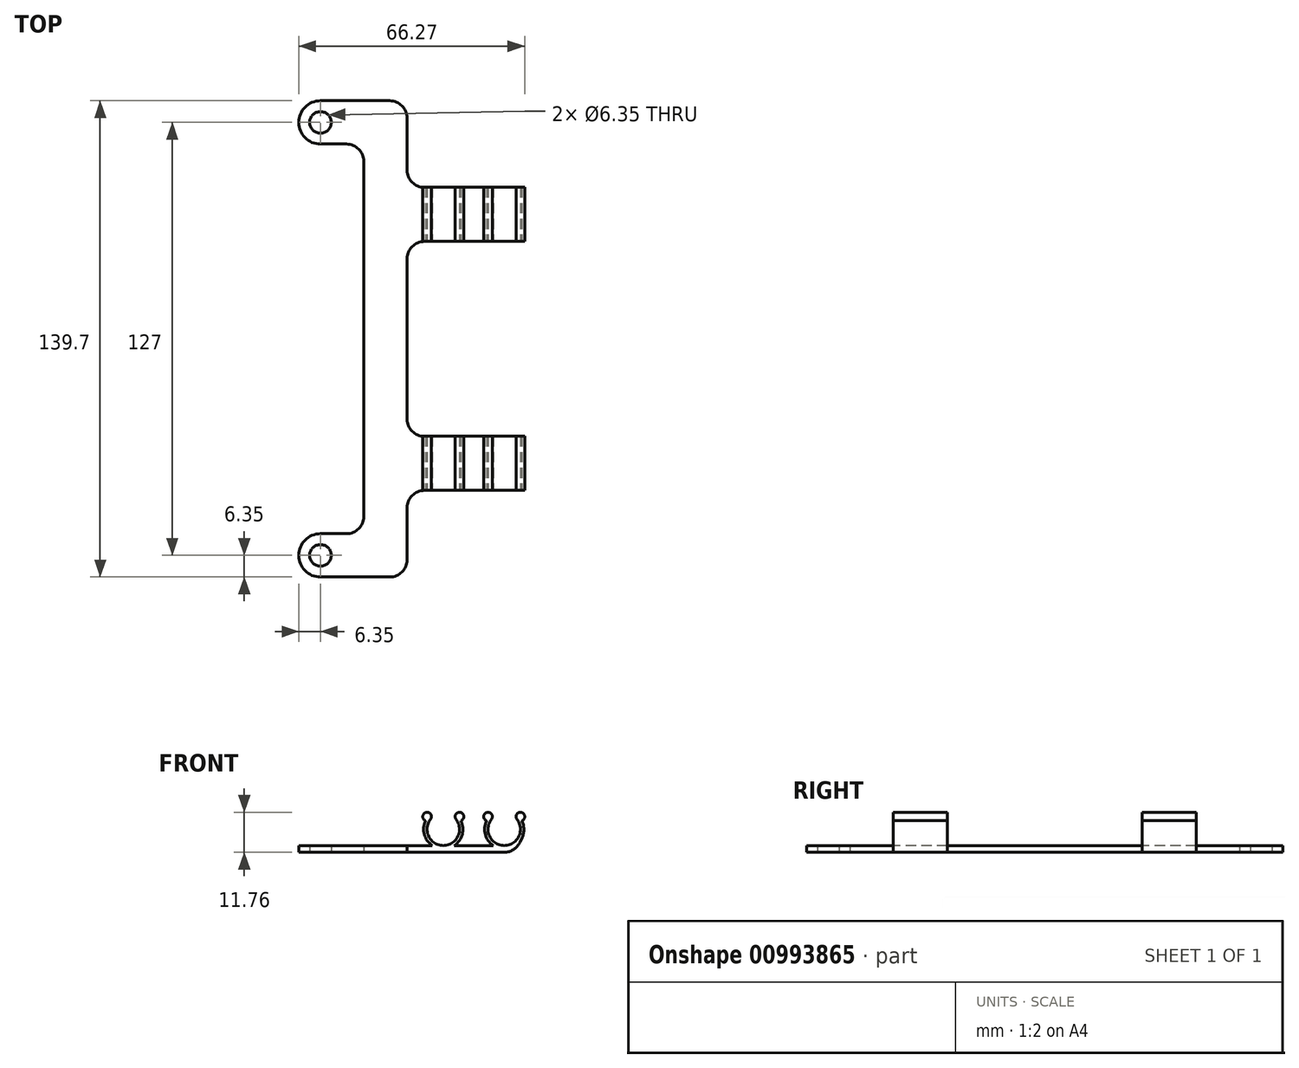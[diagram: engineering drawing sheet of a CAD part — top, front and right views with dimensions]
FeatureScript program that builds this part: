
annotation { "Feature Type Name" : "Feature", "Feature Type Description" : "" }
export const myFeature = defineFeature(function(context is Context, id is Id, definition is map)
    precondition{}
    {
        {
            var Q0;
            Q0=qCreatedBy(makeId("Top.planeOp"),FACE);
            var sketch = newSketch(context, id + "F0", { "sketchPlane" : qUnion([Q0])});
            skLineSegment(sketch, "E0", {"start": v(6.35, 0) * mm, "end": v(31.75, 0) * mm});
            skLineSegment(sketch, "E1", {"start": v(31.75, 0) * mm, "end": v(31.75, 25.4) * mm});
            skLineSegment(sketch, "E2", {"start": v(31.75, 25.4) * mm, "end": v(63.5, 25.4) * mm});
            skLineSegment(sketch, "E3", {"start": v(63.5, 25.4) * mm, "end": v(63.5, 41.28) * mm});
            skLineSegment(sketch, "E4", {"start": v(63.5, 41.28) * mm, "end": v(31.75, 41.28) * mm});
            skLineSegment(sketch, "E5", {"start": v(31.75, 41.28) * mm, "end": v(31.75, 98.42) * mm});
            skLineSegment(sketch, "E6", {"start": v(31.75, 98.42) * mm, "end": v(63.5, 98.42) * mm});
            skLineSegment(sketch, "E7", {"start": v(63.5, 98.42) * mm, "end": v(63.5, 114.3) * mm});
            skLineSegment(sketch, "E8", {"start": v(31.75, 114.3) * mm, "end": v(31.75, 139.7) * mm});
            skLineSegment(sketch, "E9", {"start": v(31.75, 139.7) * mm, "end": v(6.35, 139.7) * mm});
            skLineSegment(sketch, "E10", {"start": v(6.35, 127) * mm, "end": v(19.05, 127) * mm});
            skLineSegment(sketch, "E11", {"start": v(19.05, 127) * mm, "end": v(19.05, 12.7) * mm});
            skLineSegment(sketch, "E12", {"start": v(19.05, 12.7) * mm, "end": v(6.35, 12.7) * mm});
            skLineSegment(sketch, "E13", {"start": v(31.75, 69.85) * mm, "end": v(19.05, 69.85) * mm, "construction": true});
            skLineSegment(sketch, "E14", {"start": v(0, 133.35) * mm, "end": v(31.75, 133.35) * mm, "construction": true});
            skLineSegment(sketch, "E15", {"start": v(0, 6.35) * mm, "end": v(31.75, 6.35) * mm, "construction": true});
            skCircle(sketch, "E16", {"center": v(6.35, 133.35) * mm, "radius": 3.18 * mm});
            skArc(sketch, "E17", {"start": v(6.35, 139.7) * mm, "mid": v(0, 133.35) * mm, "end": v(6.35, 127) * mm});
            skPoint(sketch, "E18.orphan", {"position": v(0, 139.7) * mm});
            skPoint(sketch, "E19.orphan", {"position": v(0, 127) * mm});
            skArc(sketch, "E20", {"start": v(6.35, 12.7) * mm, "mid": v(0, 6.35) * mm, "end": v(6.35, 0) * mm});
            skCircle(sketch, "E21", {"center": v(6.35, 6.35) * mm, "radius": 3.18 * mm});
            skPoint(sketch, "E22.orphan", {"position": v(0, 12.7) * mm});
            skPoint(sketch, "E23.end.orphan", {"position": v(0, 0) * mm});
            skLineSegment(sketch, "E24", {"start": v(31.75, 114.3) * mm, "end": v(63.5, 114.3) * mm});
            skSolve(sketch);
        }
        {
            var Q0;
            Q0=qSketchRegion(id+"F0",true);
            extrude(context, id + "F1", {"entities" : qUnion([Q0]), "depth" : 2 * mm, "offsetDistance" : 25.4 * mm});
        }
        {
            var Q0;
            Q0=makeQuery(id+"F1.opExtrude","SWEPT_FACE",FACE,{"disambiguationData":[OSD([sQuery(id+"F0.wireOp",EDGE,"E2")])]});
            var sketch = newSketch(context, id + "F2", { "sketchPlane" : qUnion([Q0])});
            skArc(sketch, "E25", {"start": v(55.08, 9.3) * mm, "mid": v(60.26, 1) * mm, "end": v(65.43, 9.3) * mm});
            skArc(sketch, "E26", {"start": v(56.5, 9.7) * mm, "mid": v(60.26, 2) * mm, "end": v(64, 9.7) * mm});
            skLineSegment(sketch, "E27", {"start": v(60.26, 6.76) * mm, "end": v(60.26, 20.65) * mm, "construction": true});
            skLineSegment(sketch, "E28.0", {"start": v(64, 9.7) * mm, "end": v(64, 11.14) * mm, "construction": true});
            skLineSegment(sketch, "E29.0", {"start": v(56.5, 9.7) * mm, "end": v(56.5, 11.14) * mm, "construction": true});
            skArc(sketch, "E30", {"start": v(56.5, 9.7) * mm, "mid": v(55.16, 11.7) * mm, "end": v(55.08, 9.3) * mm});
            skArc(sketch, "E31.MirrorC", {"start": v(64, 9.7) * mm, "mid": v(65.35, 11.7) * mm, "end": v(65.43, 9.3) * mm});
            skLineSegment(sketch, "E32", {"start": v(51.32, 2) * mm, "end": v(51.32, 33.75) * mm, "construction": true});
            skArc(sketch, "E33.MirrorCS", {"start": v(38.63, 9.7) * mm, "mid": v(37.29, 11.7) * mm, "end": v(37.2, 9.3) * mm});
            skArc(sketch, "E34.MirrorCS", {"start": v(47.56, 9.3) * mm, "mid": v(42.38, 1) * mm, "end": v(37.2, 9.3) * mm});
            skArc(sketch, "E35.MirrorCS", {"start": v(46.13, 9.7) * mm, "mid": v(47.48, 11.7) * mm, "end": v(47.56, 9.3) * mm});
            skArc(sketch, "E36.MirrorCS", {"start": v(46.13, 9.7) * mm, "mid": v(42.38, 2) * mm, "end": v(38.63, 9.7) * mm});
            skPoint(sketch, "E37", {"position": v(51.32, 2) * mm});
            skSolve(sketch);
        }
        {
            var Q0;
            Q0=qSketchRegion(id+"F2",true);
            var Q1;
            Q1=makeQuery(id+"F1.opExtrude","SWEPT_FACE",FACE,{"disambiguationData":[OSD([sQuery(id+"F0.wireOp",EDGE,"E24")])]});
            extrude(context, id + "F3", {"entities" : qUnion([Q0]), "operationType" : NewBodyOperationType.ADD, "endBound" : BoundingType.UP_TO_SURFACE, "oppositeDirection" : true, "depth" : 25.4 * mm, "endBoundEntityFace" : qUnion([Q1]), "offsetDistance" : 25.4 * mm});
        }
        {
            var Q0;
            Q0=makeQuery(id+"F3.boolean.opBoolean","MERGE",FACE,{"derivedFrom":[makeQuery(id+"F1.opExtrude","SWEPT_FACE",FACE,{"disambiguationData":[OSD([sQuery(id+"F0.wireOp",EDGE,"E2")])]}),makeQuery(id+"F3.opExtrude","CAP_FACE",FACE,{"disambiguationData":[OSD([sQuery(id+"F2.wireOp",EDGE,"E25"),sQuery(id+"F2.wireOp",EDGE,"E26"),sQuery(id+"F2.wireOp",EDGE,"E30"),sQuery(id+"F2.wireOp",EDGE,"E31.MirrorC")])],"isStart":true}),makeQuery(id+"F3.opExtrude","CAP_FACE",FACE,{"disambiguationData":[OSD([sQuery(id+"F2.wireOp",EDGE,"E33.MirrorCS"),sQuery(id+"F2.wireOp",EDGE,"E34.MirrorCS"),sQuery(id+"F2.wireOp",EDGE,"E35.MirrorCS"),sQuery(id+"F2.wireOp",EDGE,"E36.MirrorCS")])],"isStart":true})]});
            var sketch = newSketch(context, id + "F4", { "sketchPlane" : qUnion([Q0])});
            skLineSegment(sketch, "E38", {"start": v(65.5, 4.37) * mm, "end": v(63.5, 0) * mm});
            skLineSegment(sketch, "E39", {"start": v(65.5, 4.37) * mm, "end": v(63.5, 2) * mm});
            skLineSegment(sketch, "E40", {"start": v(63.5, 2) * mm, "end": v(63.5, 0) * mm});
            skSolve(sketch);
        }
        {
            var Q0;
            Q0=qSketchRegion(id+"F4",true);
            var Q1;
            Q1=makeQuery(id+"F3.boolean.opBoolean","MERGE",FACE,{"derivedFrom":[makeQuery(id+"F1.opExtrude","SWEPT_FACE",FACE,{"disambiguationData":[OSD([sQuery(id+"F0.wireOp",EDGE,"E24")])]}),makeQuery(id+"F3.opExtrude","CAP_FACE",FACE,{"disambiguationData":[OSD([sQuery(id+"F2.wireOp",EDGE,"E25"),sQuery(id+"F2.wireOp",EDGE,"E26"),sQuery(id+"F2.wireOp",EDGE,"E30"),sQuery(id+"F2.wireOp",EDGE,"E31.MirrorC")])],"isStart":false}),makeQuery(id+"F3.opExtrude","CAP_FACE",FACE,{"disambiguationData":[OSD([sQuery(id+"F2.wireOp",EDGE,"E33.MirrorCS"),sQuery(id+"F2.wireOp",EDGE,"E34.MirrorCS"),sQuery(id+"F2.wireOp",EDGE,"E35.MirrorCS"),sQuery(id+"F2.wireOp",EDGE,"E36.MirrorCS")])],"isStart":false})]});
            extrude(context, id + "F5", {"entities" : qUnion([Q0]), "operationType" : NewBodyOperationType.ADD, "endBound" : BoundingType.UP_TO_SURFACE, "oppositeDirection" : true, "depth" : 25.4 * mm, "endBoundEntityFace" : qUnion([Q1]), "offsetDistance" : 25.4 * mm});
        }
        {
            var Q0;
            Q0=makeQuery(id+"F1.opExtrude","CAP_FACE",FACE,{"disambiguationData":[OSD([sQuery(id+"F0.wireOp",EDGE,"E0"),sQuery(id+"F0.wireOp",EDGE,"E1"),sQuery(id+"F0.wireOp",EDGE,"E2"),sQuery(id+"F0.wireOp",EDGE,"E3"),sQuery(id+"F0.wireOp",EDGE,"E4"),sQuery(id+"F0.wireOp",EDGE,"E5"),sQuery(id+"F0.wireOp",EDGE,"E6"),sQuery(id+"F0.wireOp",EDGE,"E7"),sQuery(id+"F0.wireOp",EDGE,"E8"),sQuery(id+"F0.wireOp",EDGE,"E9"),sQuery(id+"F0.wireOp",EDGE,"E10"),sQuery(id+"F0.wireOp",EDGE,"E11"),sQuery(id+"F0.wireOp",EDGE,"E12"),sQuery(id+"F0.wireOp",EDGE,"E16"),sQuery(id+"F0.wireOp",EDGE,"E17"),sQuery(id+"F0.wireOp",EDGE,"E20"),sQuery(id+"F0.wireOp",EDGE,"E21"),sQuery(id+"F0.wireOp",EDGE,"E24")])],"isStart":true});
            var sketch = newSketch(context, id + "F6", { "sketchPlane" : qUnion([Q0])});
            skLineSegment(sketch, "E41.bottom", {"start": v(31.75, -41.28) * mm, "end": v(76.2, -41.28) * mm});
            skLineSegment(sketch, "E41.top", {"start": v(31.75, -98.42) * mm, "end": v(76.2, -98.42) * mm});
            skLineSegment(sketch, "E41.left", {"start": v(31.75, -41.28) * mm, "end": v(31.75, -98.42) * mm});
            skLineSegment(sketch, "E41.right", {"start": v(76.2, -41.28) * mm, "end": v(76.2, -98.42) * mm});
            skSolve(sketch);
        }
        {
            var Q0;
            Q0=qSketchRegion(id+"F6",true);
            extrude(context, id + "F7", {"entities" : qUnion([Q0]), "operationType" : NewBodyOperationType.REMOVE, "oppositeDirection" : true, "depth" : 25.4 * mm, "offsetDistance" : 25.4 * mm});
        }
        {
            var Q0;
            {var subQ0=sQuery(id+"F0.wireOp",EDGE,"E11");var subQ1=sQuery(id+"F2.wireOp",EDGE,"E34.MirrorCS");var subQ2=sQuery(id+"F0.wireOp",EDGE,"E10");var subQ3=sQuery(id+"F2.wireOp",EDGE,"E36.MirrorCS");var subQ4=sQuery(id+"F2.wireOp",EDGE,"E35.MirrorCS");var subQ5=sQuery(id+"F2.wireOp",EDGE,"E33.MirrorCS");var subQ6=sQuery(id+"F0.wireOp",EDGE,"E8");var subQ7=sQuery(id+"F0.wireOp",EDGE,"E6");var subQ8=sQuery(id+"F0.wireOp",EDGE,"E5");var subQ9=sQuery(id+"F0.wireOp",EDGE,"E9");var subQ10=sQuery(id+"F0.wireOp",EDGE,"E0");var subQ11=sQuery(id+"F0.wireOp",EDGE,"E1");var subQ12=sQuery(id+"F0.wireOp",EDGE,"E2");var subQ13=sQuery(id+"F0.wireOp",EDGE,"E4");var subQ14=sQuery(id+"F2.wireOp",EDGE,"E31.MirrorC");var subQ15=sQuery(id+"F2.wireOp",EDGE,"E30");var subQ16=sQuery(id+"F2.wireOp",EDGE,"E26");var subQ17=sQuery(id+"F2.wireOp",EDGE,"E25");var subQ18=sQuery(id+"F0.wireOp",EDGE,"E12");var subQ19=sQuery(id+"F0.wireOp",EDGE,"E16");var subQ20=sQuery(id+"F0.wireOp",EDGE,"E17");var subQ21=sQuery(id+"F0.wireOp",EDGE,"E20");var subQ22=sQuery(id+"F0.wireOp",EDGE,"E21");var subQ23=sQuery(id+"F0.wireOp",EDGE,"E24");Q0=makeQuery(id+"F3.boolean.opBoolean","SPLIT",FACE,{"disambiguationData":[TD([makeQuery(id+"F1.opExtrude","SWEPT_FACE",FACE,{"disambiguationData":[OSD([subQ10])]}),makeQuery(id+"F1.opExtrude","SWEPT_FACE",FACE,{"disambiguationData":[OSD([subQ11])]}),makeQuery(id+"F1.opExtrude","SWEPT_FACE",FACE,{"disambiguationData":[OSD([subQ12])]}),makeQuery(id+"F1.opExtrude","SWEPT_FACE",FACE,{"disambiguationData":[OSD([subQ13])]}),makeQuery(id+"F1.opExtrude","SWEPT_FACE",FACE,{"disambiguationData":[OSD([subQ8])]}),makeQuery(id+"F1.opExtrude","SWEPT_FACE",FACE,{"disambiguationData":[OSD([subQ7])]}),makeQuery(id+"F1.opExtrude","SWEPT_FACE",FACE,{"disambiguationData":[OSD([subQ6])]}),makeQuery(id+"F1.opExtrude","SWEPT_FACE",FACE,{"disambiguationData":[OSD([subQ9])]}),makeQuery(id+"F1.opExtrude","SWEPT_FACE",FACE,{"disambiguationData":[OSD([subQ2])]}),makeQuery(id+"F1.opExtrude","SWEPT_FACE",FACE,{"disambiguationData":[OSD([subQ0])]}),makeQuery(id+"F1.opExtrude","SWEPT_FACE",FACE,{"disambiguationData":[OSD([subQ18])]}),makeQuery(id+"F1.opExtrude","SWEPT_FACE",FACE,{"disambiguationData":[OSD([subQ19])]}),makeQuery(id+"F1.opExtrude","SWEPT_FACE",FACE,{"disambiguationData":[OSD([subQ20])]}),makeQuery(id+"F1.opExtrude","SWEPT_FACE",FACE,{"disambiguationData":[OSD([subQ21])]}),makeQuery(id+"F1.opExtrude","SWEPT_FACE",FACE,{"disambiguationData":[OSD([subQ22])]}),makeQuery(id+"F1.opExtrude","SWEPT_FACE",FACE,{"disambiguationData":[OSD([subQ23])]}),makeQuery(id+"F3.opExtrude","CAP_FACE",FACE,{"disambiguationData":[OSD([subQ17,subQ16,subQ15,subQ14])],"isStart":true}),makeQuery(id+"F3.opExtrude","CAP_FACE",FACE,{"disambiguationData":[OSD([subQ17,subQ16,subQ15,subQ14])],"isStart":false}),makeQuery(id+"F3.opExtrude","CAP_FACE",FACE,{"disambiguationData":[OSD([subQ5,subQ1,subQ4,subQ3])],"isStart":true}),makeQuery(id+"F3.opExtrude","CAP_FACE",FACE,{"disambiguationData":[OSD([subQ5,subQ1,subQ4,subQ3])],"isStart":false}),makeQuery(id+"F3.opExtrude","SWEPT_FACE",FACE,{"disambiguationData":[OSD([subQ1])]})])],"derivedFrom":makeQuery(id+"F1.opExtrude","CAP_FACE",FACE,{"disambiguationData":[OSD([subQ10,subQ11,subQ12,sQuery(id+"F0.wireOp",EDGE,"E3"),subQ13,subQ8,subQ7,sQuery(id+"F0.wireOp",EDGE,"E7"),subQ6,subQ9,subQ2,subQ0,subQ18,subQ19,subQ20,subQ21,subQ22,subQ23])],"isStart":false})});}
            var sketch = newSketch(context, id + "F8", { "sketchPlane" : qUnion([Q0])});
            skLineSegment(sketch, "E42.bottom", {"start": v(63.5, 41.28) * mm, "end": v(19.05, 41.28) * mm});
            skLineSegment(sketch, "E42.top", {"start": v(63.5, 98.42) * mm, "end": v(19.05, 98.42) * mm});
            skLineSegment(sketch, "E42.left", {"start": v(63.5, 41.28) * mm, "end": v(63.5, 98.42) * mm});
            skLineSegment(sketch, "E42.right", {"start": v(19.05, 41.28) * mm, "end": v(19.05, 98.42) * mm});
            skPoint(sketch, "E42.middle", {"position": v(41.28, 69.85) * mm});
            skSolve(sketch);
        }
        {
            var Q0;
            Q0=qSketchRegion(id+"F8",true);
            extrude(context, id + "F9", {"entities" : qUnion([Q0]), "operationType" : NewBodyOperationType.REMOVE, "depth" : 25.4 * mm, "offsetDistance" : 25.4 * mm});
        }
        {
            var Q0;
            Q0=makeQuery(id+"F3.boolean.opBoolean","MERGE",FACE,{"derivedFrom":[makeQuery(id+"F1.opExtrude","SWEPT_FACE",FACE,{"disambiguationData":[OSD([sQuery(id+"F0.wireOp",EDGE,"E2")])]}),makeQuery(id+"F3.opExtrude","CAP_FACE",FACE,{"disambiguationData":[OSD([sQuery(id+"F2.wireOp",EDGE,"E25"),sQuery(id+"F2.wireOp",EDGE,"E26"),sQuery(id+"F2.wireOp",EDGE,"E30"),sQuery(id+"F2.wireOp",EDGE,"E31.MirrorC")])],"isStart":true}),makeQuery(id+"F3.opExtrude","CAP_FACE",FACE,{"disambiguationData":[OSD([sQuery(id+"F2.wireOp",EDGE,"E33.MirrorCS"),sQuery(id+"F2.wireOp",EDGE,"E34.MirrorCS"),sQuery(id+"F2.wireOp",EDGE,"E35.MirrorCS"),sQuery(id+"F2.wireOp",EDGE,"E36.MirrorCS")])],"isStart":true})]});
            var sketch = newSketch(context, id + "F10", { "sketchPlane" : qUnion([Q0])});
            skCircle(sketch, "E43", {"center": v(42.38, 6.76) * mm, "radius": 4.76 * mm});
            skCircle(sketch, "E44", {"center": v(60.26, 6.76) * mm, "radius": 4.76 * mm});
            skSolve(sketch);
        }
        {
            var Q0;
            Q0=qSketchRegion(id+"F10",true);
            var Q1;
            Q1=makeQuery(id+"F3.boolean.opBoolean","MERGE",FACE,{"derivedFrom":[makeQuery(id+"F1.opExtrude","SWEPT_FACE",FACE,{"disambiguationData":[OSD([sQuery(id+"F0.wireOp",EDGE,"E24")])]}),makeQuery(id+"F3.opExtrude","CAP_FACE",FACE,{"disambiguationData":[OSD([sQuery(id+"F2.wireOp",EDGE,"E25"),sQuery(id+"F2.wireOp",EDGE,"E26"),sQuery(id+"F2.wireOp",EDGE,"E30"),sQuery(id+"F2.wireOp",EDGE,"E31.MirrorC")])],"isStart":false}),makeQuery(id+"F3.opExtrude","CAP_FACE",FACE,{"disambiguationData":[OSD([sQuery(id+"F2.wireOp",EDGE,"E33.MirrorCS"),sQuery(id+"F2.wireOp",EDGE,"E34.MirrorCS"),sQuery(id+"F2.wireOp",EDGE,"E35.MirrorCS"),sQuery(id+"F2.wireOp",EDGE,"E36.MirrorCS")])],"isStart":false})]});
            extrude(context, id + "F11", {"entities" : qUnion([Q0]), "operationType" : NewBodyOperationType.REMOVE, "endBound" : BoundingType.UP_TO_SURFACE, "oppositeDirection" : true, "depth" : 25.4 * mm, "endBoundEntityFace" : qUnion([Q1]), "offsetDistance" : 25.4 * mm});
        }
        {
            var Q0;
            Q0=makeQuery(id+"F1.opExtrude","SWEPT_EDGE",EDGE,{"disambiguationData":[OSD([sQuery(id+"F0.wireOp",EDGE,"E0"),sQuery(id+"F0.wireOp",EDGE,"E1")])]});
            var Q1;
            Q1=makeQuery(id+"F1.opExtrude","SWEPT_EDGE",EDGE,{"disambiguationData":[OSD([sQuery(id+"F0.wireOp",EDGE,"E1"),sQuery(id+"F0.wireOp",EDGE,"E2")])]});
            var Q2;
            Q2=makeQuery(id+"F1.opExtrude","SWEPT_EDGE",EDGE,{"disambiguationData":[OSD([sQuery(id+"F0.wireOp",EDGE,"E4"),sQuery(id+"F0.wireOp",EDGE,"E5")])]});
            var Q3;
            Q3=makeQuery(id+"F1.opExtrude","SWEPT_EDGE",EDGE,{"disambiguationData":[OSD([sQuery(id+"F0.wireOp",EDGE,"E5"),sQuery(id+"F0.wireOp",EDGE,"E6")])]});
            var Q4;
            Q4=makeQuery(id+"F1.opExtrude","SWEPT_EDGE",EDGE,{"disambiguationData":[OSD([sQuery(id+"F0.wireOp",EDGE,"E8"),sQuery(id+"F0.wireOp",EDGE,"E24")])]});
            var Q5;
            Q5=makeQuery(id+"F1.opExtrude","SWEPT_EDGE",EDGE,{"disambiguationData":[OSD([sQuery(id+"F0.wireOp",EDGE,"E8"),sQuery(id+"F0.wireOp",EDGE,"E9")])]});
            var Q6;
            Q6=makeQuery(id+"F1.opExtrude","SWEPT_EDGE",EDGE,{"disambiguationData":[OSD([sQuery(id+"F0.wireOp",EDGE,"E10"),sQuery(id+"F0.wireOp",EDGE,"E11")])]});
            var Q7;
            Q7=makeQuery(id+"F1.opExtrude","SWEPT_EDGE",EDGE,{"disambiguationData":[OSD([sQuery(id+"F0.wireOp",EDGE,"E11"),sQuery(id+"F0.wireOp",EDGE,"E12")])]});
            fillet(context, id + "F12", {"entities" : qUnion([Q0, Q1, Q2, Q3, Q4, Q5, Q6, Q7]), "radius" : 5.08 * mm, "tangentPropagation" : true, "allowEdgeOverflow" : false});
        }
        {
            var Q0;
            Q0=makeQuery(id+"F5.boolean.opBoolean","MERGE",EDGE,{"derivedFrom":[makeQuery(id+"F1.opExtrude","CAP_EDGE",EDGE,{"disambiguationData":[OSD([sQuery(id+"F0.wireOp",EDGE,"E3")])],"isStart":true}),makeQuery(id+"F5.opExtrude","SWEPT_EDGE",EDGE,{"disambiguationData":[OSD([sQuery(id+"F0.wireOp",EDGE,"E2"),sQuery(id+"F4.wireOp",EDGE,"E38"),sQuery(id+"F4.wireOp",EDGE,"E40")])]})]});
            var Q1;
            Q1=makeQuery(id+"F5.boolean.opBoolean","MERGE",EDGE,{"derivedFrom":[makeQuery(id+"F1.opExtrude","CAP_EDGE",EDGE,{"disambiguationData":[OSD([sQuery(id+"F0.wireOp",EDGE,"E7")])],"isStart":true}),makeQuery(id+"F5.opExtrude","SWEPT_EDGE",EDGE,{"disambiguationData":[OSD([sQuery(id+"F0.wireOp",EDGE,"E2"),sQuery(id+"F4.wireOp",EDGE,"E38"),sQuery(id+"F4.wireOp",EDGE,"E40")])]})]});
            fillet(context, id + "F13", {"entities" : qUnion([Q0, Q1]), "radius" : 5.08 * mm, "tangentPropagation" : true, "allowEdgeOverflow" : false});
        }
    });
